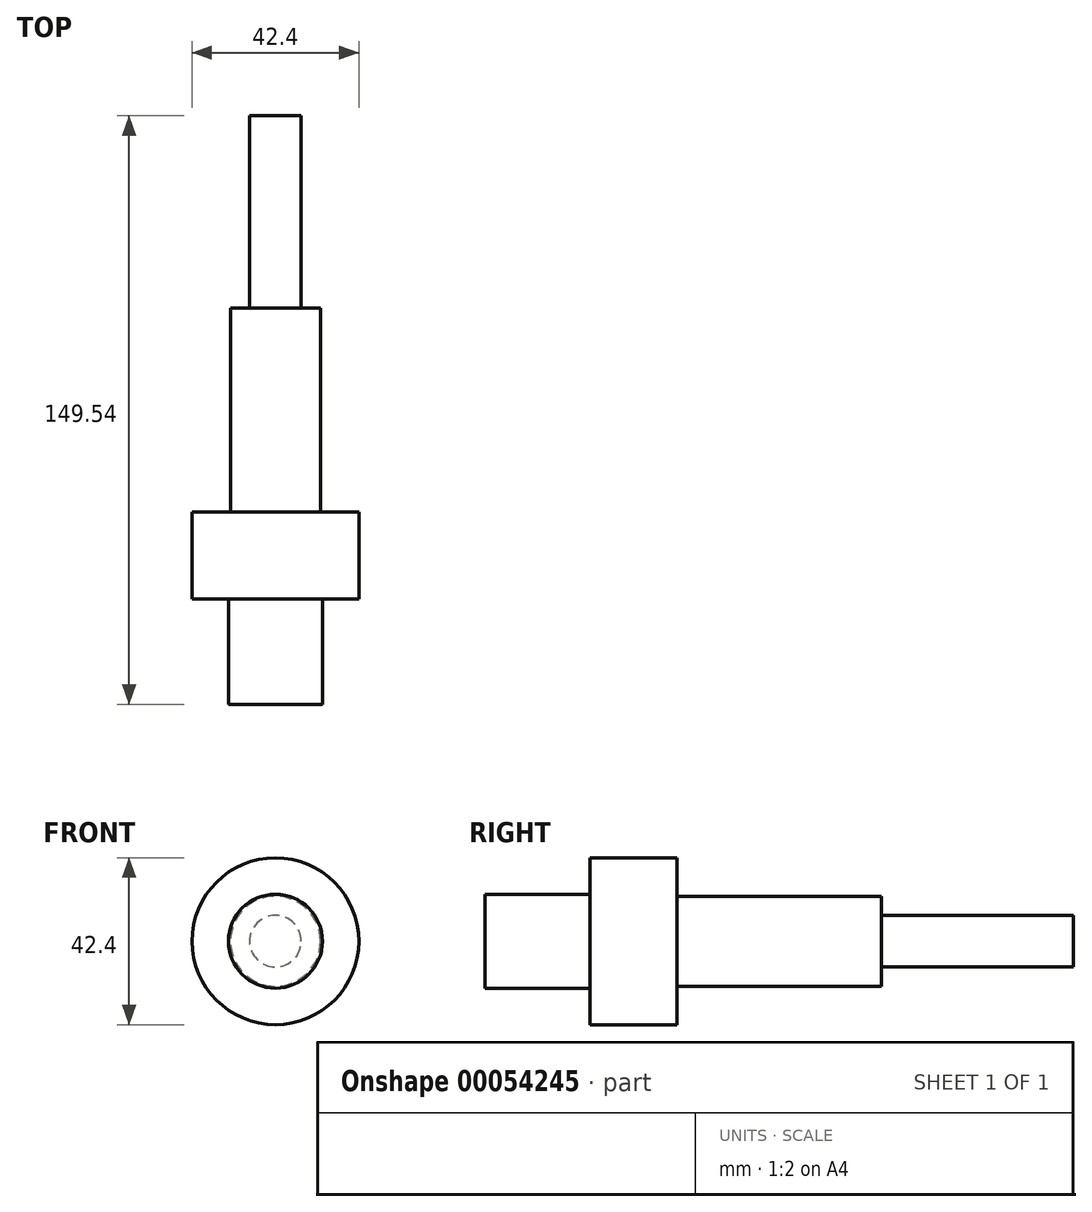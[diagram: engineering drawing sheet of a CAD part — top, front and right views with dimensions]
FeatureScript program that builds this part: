
annotation { "Feature Type Name" : "Feature", "Feature Type Description" : "" }
export const myFeature = defineFeature(function(context is Context, id is Id, definition is map)
    precondition{}
    {
        {
            var Q0;
            Q0=qCreatedBy(makeId("Right.planeOp"),FACE);
            var sketch = newSketch(context, id + "F0", { "sketchPlane" : qUnion([Q0])});
            skLineSegment(sketch, "E0", {"start": v(-74.9, 11.95) * mm, "end": v(-48.17, 11.95) * mm});
            skLineSegment(sketch, "E1", {"start": v(-48.17, 11.95) * mm, "end": v(-48.17, 21.2) * mm});
            skLineSegment(sketch, "E2", {"start": v(-48.17, 21.2) * mm, "end": v(-26.08, 21.2) * mm});
            skLineSegment(sketch, "E3", {"start": v(-26.08, 21.2) * mm, "end": v(-26.08, 11.43) * mm});
            skLineSegment(sketch, "E4", {"start": v(-26.08, 11.43) * mm, "end": v(25.82, 11.43) * mm});
            skLineSegment(sketch, "E5", {"start": v(25.82, 11.43) * mm, "end": v(25.82, 6.55) * mm});
            skLineSegment(sketch, "E6", {"start": v(25.82, 6.55) * mm, "end": v(74.64, 6.55) * mm});
            skLineSegment(sketch, "E7", {"start": v(74.64, 6.55) * mm, "end": v(74.64, 0) * mm});
            skLineSegment(sketch, "E8", {"start": v(74.64, 0) * mm, "end": v(-74.9, 0) * mm});
            skLineSegment(sketch, "E9", {"start": v(-74.9, 0) * mm, "end": v(-74.9, 11.95) * mm});
            skSolve(sketch);
        }
        {
            var Q0;
            Q0=makeQuery(id+"F0.imprint","IMPRINT",FACE,{"disambiguationData":[TD([[makeQuery(id+"F0.imprint","IMPRINT",EDGE,{"derivedFrom":sQuery(id+"F0.wireOp",EDGE,"E0")}),-1.0]])]});
            var Q1;
            Q1=sQuery(id+"F0.wireOp",EDGE,"E8");
            revolve(context, id + "F1", {"entities" : qUnion([Q0]), "axis" : qUnion([Q1]), "revolveType" : RevolveType.FULL});
        }
    });
